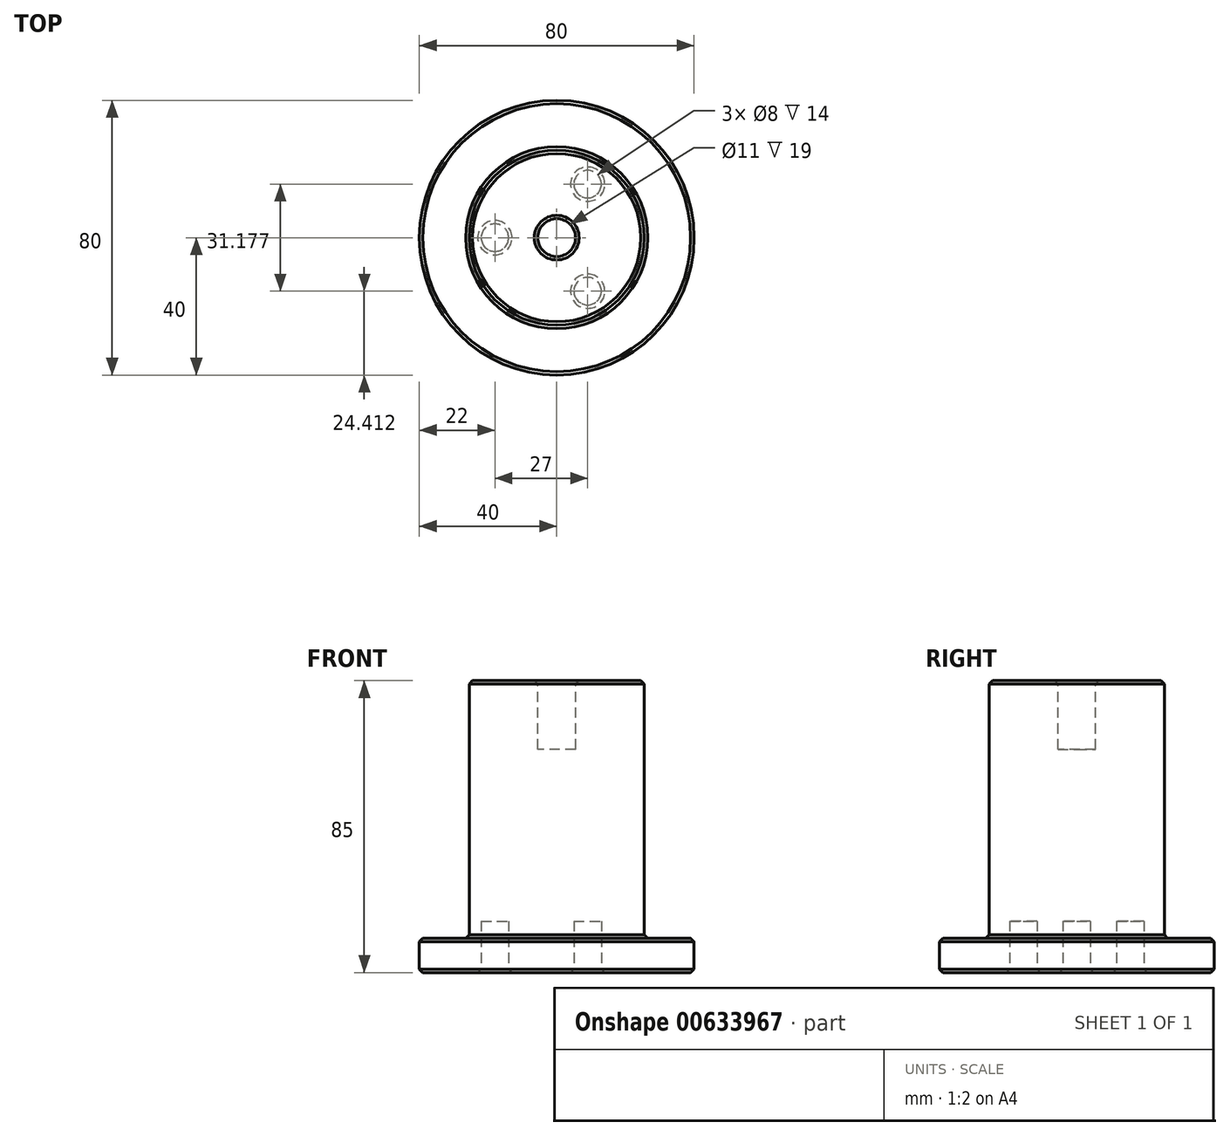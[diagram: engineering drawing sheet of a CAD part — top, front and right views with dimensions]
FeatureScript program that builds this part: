
annotation { "Feature Type Name" : "Feature", "Feature Type Description" : "" }
export const myFeature = defineFeature(function(context is Context, id is Id, definition is map)
    precondition{}
    {
        {
            var Q0;
            Q0=qCreatedBy(makeId("Top.planeOp"),FACE);
            var sketch = newSketch(context, id + "F0", { "sketchPlane" : qUnion([Q0])});
            skCircle(sketch, "E0", {"center": v(0, 0) * mm, "radius": 40 * mm});
            skSolve(sketch);
        }
        {
            var Q0;
            Q0=makeQuery(id+"F0.imprint","IMPRINT",FACE,{"disambiguationData":[TD([[makeQuery(id+"F0.imprint","IMPRINT",EDGE,{"derivedFrom":sQuery(id+"F0.wireOp",EDGE,"E0")}),1.0]])]});
            extrude(context, id + "F1", {"entities" : qUnion([Q0]), "flatOperationType" : FlatOperationType.REMOVE, "depth" : 10 * mm, "offsetDistance" : 25 * mm, "domain" : OperationDomain.MODEL});
        }
        {
            var Q0;
            Q0=makeQuery(id+"F1.opExtrude","CAP_FACE",FACE,{"disambiguationData":[OSD([sQuery(id+"F0.wireOp",EDGE,"E0")])],"isStart":false});
            var sketch = newSketch(context, id + "F2", { "sketchPlane" : qUnion([Q0])});
            skCircle(sketch, "E1", {"center": v(0, 0) * mm, "radius": 25.5 * mm});
            skSolve(sketch);
        }
        {
            var Q0;
            Q0=makeQuery(id+"F2.imprint","IMPRINT",FACE,{"disambiguationData":[TD([[makeQuery(id+"F2.imprint","IMPRINT",EDGE,{"derivedFrom":sQuery(id+"F2.wireOp",EDGE,"E1")}),1.0]])]});
            extrude(context, id + "F3", {"entities" : qUnion([Q0]), "operationType" : NewBodyOperationType.ADD, "depth" : 75 * mm, "offsetDistance" : 25 * mm});
        }
        {
            var Q0;
            Q0=makeQuery(id+"F1.opExtrude","CAP_FACE",FACE,{"disambiguationData":[OSD([sQuery(id+"F0.wireOp",EDGE,"E0")])],"isStart":true});
            var sketch = newSketch(context, id + "F4", { "sketchPlane" : qUnion([Q0])});
            skLineSegment(sketch, "E2", {"start": v(0, 0) * mm, "end": v(-18, 0) * mm, "construction": true});
            skCircle(sketch, "E3", {"center": v(-18, 0) * mm, "radius": 4 * mm});
            skCircle(sketch, "E4.1.0", {"center": v(9, -15.59) * mm, "radius": 4 * mm});
            skCircle(sketch, "E4.2.0", {"center": v(9, 15.59) * mm, "radius": 4 * mm});
            skPoint(sketch, "E4.center", {"position": v(0, 0) * mm});
            skSolve(sketch);
        }
        {
            var Q0;
            Q0=makeQuery(id+"F4.imprint","IMPRINT",FACE,{"disambiguationData":[TD([[makeQuery(id+"F4.imprint","IMPRINT",EDGE,{"derivedFrom":sQuery(id+"F4.wireOp",EDGE,"E4.2.0")}),1.0]])]});
            var Q1;
            Q1=makeQuery(id+"F4.imprint","IMPRINT",FACE,{"disambiguationData":[TD([[makeQuery(id+"F4.imprint","IMPRINT",EDGE,{"derivedFrom":sQuery(id+"F4.wireOp",EDGE,"E4.1.0")}),1.0]])]});
            var Q2;
            Q2=makeQuery(id+"F4.imprint","IMPRINT",FACE,{"disambiguationData":[TD([[makeQuery(id+"F4.imprint","IMPRINT",EDGE,{"derivedFrom":sQuery(id+"F4.wireOp",EDGE,"E3")}),1.0]])]});
            extrude(context, id + "F5", {"entities" : qUnion([Q0, Q1, Q2]), "operationType" : NewBodyOperationType.REMOVE, "flatOperationType" : FlatOperationType.REMOVE, "oppositeDirection" : true, "depth" : 15 * mm, "offsetDistance" : 25 * mm, "domain" : OperationDomain.MODEL});
        }
        {
            var Q0;
            Q0=makeQuery(id+"F3.opExtrude","CAP_FACE",FACE,{"disambiguationData":[OSD([sQuery(id+"F2.wireOp",EDGE,"E1")])],"isStart":false});
            var sketch = newSketch(context, id + "F6", { "sketchPlane" : qUnion([Q0])});
            skCircle(sketch, "E5", {"center": v(0, 0) * mm, "radius": 5.5 * mm});
            skSolve(sketch);
        }
        {
            var Q0;
            Q0=makeQuery(id+"F6.imprint","IMPRINT",FACE,{"disambiguationData":[TD([[makeQuery(id+"F6.imprint","IMPRINT",EDGE,{"derivedFrom":sQuery(id+"F6.wireOp",EDGE,"E5")}),1.0]])]});
            var Q1;
            Q1=sQuery(id+"F6.wireOp",EDGE,"E5");
            extrude(context, id + "F7", {"entities" : qUnion([Q0]), "operationType" : NewBodyOperationType.REMOVE, "surfaceEntities" : qUnion([Q1]), "oppositeDirection" : true, "depth" : 20 * mm, "offsetDistance" : 25 * mm});
        }
        {
            var Q0;
            Q0=makeQuery(id+"F1.opExtrude","CAP_FACE",FACE,{"disambiguationData":[OSD([sQuery(id+"F0.wireOp",EDGE,"E0")])],"isStart":true});
            var Q1;
            Q1=makeQuery(id+"F1.opExtrude","CAP_FACE",FACE,{"disambiguationData":[OSD([sQuery(id+"F0.wireOp",EDGE,"E0")])],"isStart":false});
            var Q2;
            Q2=makeQuery(id+"F3.opExtrude","CAP_FACE",FACE,{"disambiguationData":[OSD([sQuery(id+"F2.wireOp",EDGE,"E1")])],"isStart":false});
            chamfer(context, id + "F8", {"entities" : qUnion([Q0, Q1, Q2]), "width" : 1 * mm, "tangentPropagation" : true});
        }
    });
